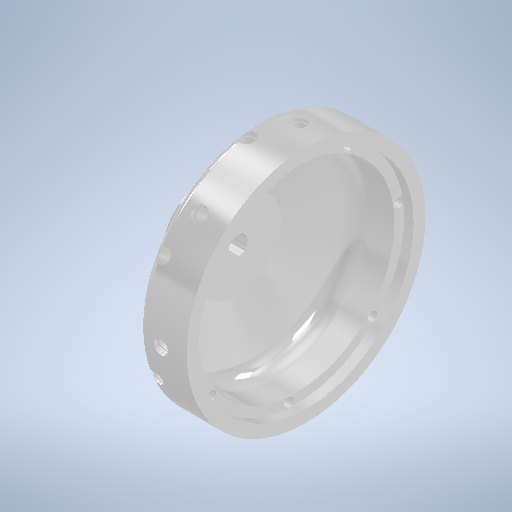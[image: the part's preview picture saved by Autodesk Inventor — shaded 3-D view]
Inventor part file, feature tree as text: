
AUTODESK INVENTOR PART (.ipt)
format: ipt  version: 2025 (Build 290162010, 162A)  size: 524,800 bytes
history: native  units: mm
features: sketch x6, hole x4, pattern_circular x3, revolve x2, plane x2, projected_geometry x1
ambient origin geometry x8: Origin, YZ Plane, XZ Plane, XY Plane, X Axis, Y Axis, Z Axis, Center Point
bodies: Volumenkörper1 (feature_tree)
feature tree (18):
  revolve  "Umdrehung1"
  revolve  "Umdrehung2"
  hole  "Bohrung1"  [1 undecoded]
  plane  "Arbeitsebene1"
  plane  "Arbeitsebene2"
  hole  "Bohrung2"  [1 undecoded]
  pattern_circular  "Runde Anordnung1"  [2 undecoded]
  hole  "Bohrung3"  [1 undecoded]
  pattern_circular  "Runde Anordnung2"  [2 undecoded]
  hole  "Bohrung4"  [1 undecoded]
  pattern_circular  "Runde Anordnung3"  Count=9  [1 undecoded]
  sketch  "Skizze1"  dims[d1=42.0mm d2=8.0mm]
  sketch  "Skizze2"  dims[d3=3.0mm d4=100.0mm]
  sketch  "Skizze3"  dims[d5=36.0mm]
  sketch  "Skizze5"  dims[d7=19.0mm]
  projected_geometry  "Projizierte Kontur1"
  sketch  "Skizze7"  dims[d8=35.0mm]
  sketch  "Skizze8"  dims[d10=90.0deg d11=4.0mm d12=8.0mm d13=3.5mm d14=82.0mm d15=90.0mm d16=3.5mm d17=90.0deg d18=8.0mm d19=6.0mm d20=28.0mm d21=8.0mm d22=90.0deg d23=8.0mm d24=0.0mm d25=50.0mm d26=-22.9mm d28=4.0mm d29=6.0mm d30=7.0mm d31=2.3mm d32=90.0deg d33=8.0mm d34=0.0mm d36=86.5mm d37=30.0deg d38=70.0mm d39=360.0deg d41=16.5mm d42=8.0mm d43=5.0mm d44=6.0mm d45=6.0mm d46=2.3mm d47=90.0deg d48=9.0mm d49=0.0mm d50=70.0mm d51=360.0deg d53=16.0mm d54=11.0mm d55=5.0mm d56=6.0mm d57=6.0mm d58=2.3mm d59=90.0deg d60=9.0mm d61=0.0mm d62=70.0mm d63=360.0deg]
note: 9 required parameter values undecoded (feature->parameter linkage not recoverable at this tier; creation-order binding heuristic only, values carry confidence <= 0.55)
